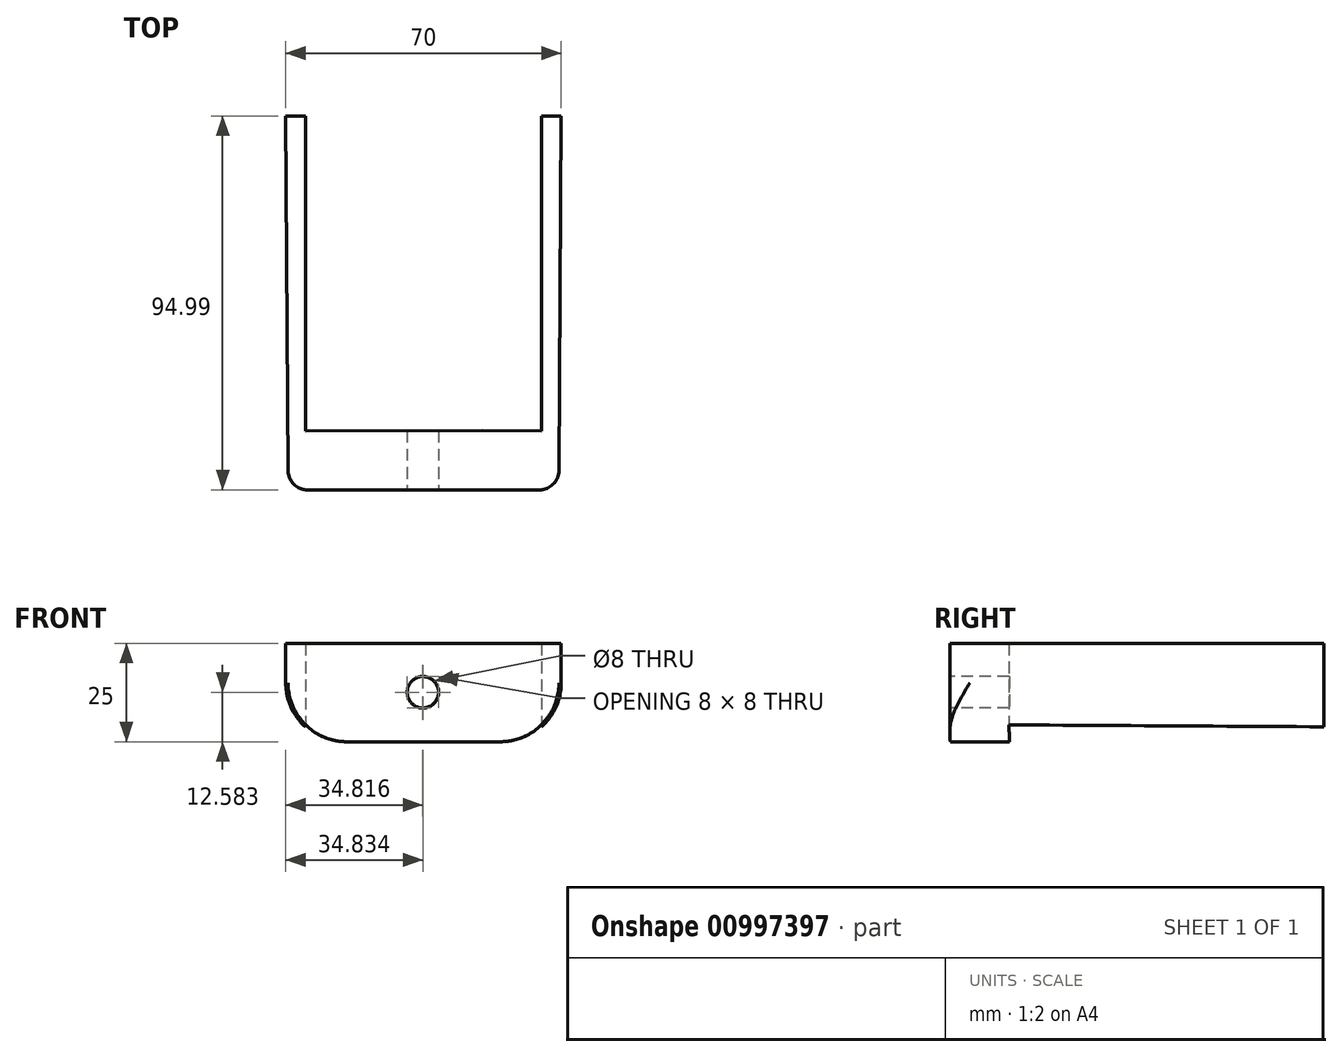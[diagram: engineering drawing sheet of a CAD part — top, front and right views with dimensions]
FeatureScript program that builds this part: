
annotation { "Feature Type Name" : "Feature", "Feature Type Description" : "" }
export const myFeature = defineFeature(function(context is Context, id is Id, definition is map)
    precondition{}
    {
        {
            var Q0;
            Q0=qCreatedBy(makeId("Top.planeOp"),FACE);
            var sketch = newSketch(context, id + "F0", { "sketchPlane" : qUnion([Q0])});
            skLineSegment(sketch, "E0.left", {"start": v(9.87, 79.3) * mm, "end": v(10.45, 169.3) * mm});
            skPoint(sketch, "E1.visualSharp", {"position": v(9.46, 15.57) * mm});
            skArc(sketch, "E1.filletArc", {"start": v(4.87, 74.34) * mm, "mid": v(8.4, 75.79) * mm, "end": v(9.87, 79.3) * mm});
            skLineSegment(sketch, "E2", {"start": v(10.45, 169.3) * mm, "end": v(5.45, 169.33) * mm});
            skLineSegment(sketch, "E3", {"start": v(5.45, 169.33) * mm, "end": v(5.45, 89.33) * mm});
            skLineSegment(sketch, "E4.MirrorCS", {"start": v(-9.55, 89.37) * mm, "end": v(5.45, 89.33) * mm});
            skLineSegment(sketch, "E5", {"start": v(4.87, 74.34) * mm, "end": v(-9.55, 74.37) * mm});
            skLineSegment(sketch, "E6.MirrorCS", {"start": v(-58.97, 79.3) * mm, "end": v(-59.55, 169.3) * mm});
            skPoint(sketch, "E7.MirrorP", {"position": v(-28.57, 15.57) * mm});
            skLineSegment(sketch, "E8.MirrorCS", {"start": v(-59.55, 169.3) * mm, "end": v(-54.55, 169.33) * mm});
            skLineSegment(sketch, "E9.MirrorCS", {"start": v(-54.55, 169.33) * mm, "end": v(-54.55, 89.33) * mm});
            skArc(sketch, "E10.MirrorCS", {"start": v(-53.98, 74.34) * mm, "mid": v(-57.5, 75.79) * mm, "end": v(-58.97, 79.3) * mm});
            skLineSegment(sketch, "E11.MirrorCS", {"start": v(-53.98, 74.34) * mm, "end": v(-39.55, 74.37) * mm});
            skLineSegment(sketch, "E12.MirrorCS", {"start": v(-9.55, 89.37) * mm, "end": v(-54.55, 89.33) * mm});
            skLineSegment(sketch, "E13", {"start": v(-39.55, 74.37) * mm, "end": v(-9.55, 74.37) * mm});
            skSolve(sketch);
        }
        {
            var Q0;
            {var subQ5=sQuery(id+"F0.wireOp",EDGE,"E1.filletArc");Q0=makeQuery(id+"F0.imprint","IMPRINT",FACE,{"disambiguationData":[TD([[makeQuery(id+"F0.imprint","IMPRINT",EDGE,{"derivedFrom":subQ5}),1.0]])]});}
            var Q1;
            {var subQ2=sQuery(id+"F0.wireOp",EDGE,"E0.left");Q1=makeQuery(id+"F0.imprint","IMPRINT",FACE,{"disambiguationData":[TD([[makeQuery(id+"F0.imprint","IMPRINT",EDGE,{"derivedFrom":subQ2}),1.0]])]});}
            var Q2;
            {var subQ3=sQuery(id+"F0.wireOp",EDGE,"E6.MirrorCS");Q2=makeQuery(id+"F0.imprint","IMPRINT",FACE,{"disambiguationData":[TD([[makeQuery(id+"F0.imprint","IMPRINT",EDGE,{"derivedFrom":subQ3}),-1.0]])]});}
            var Q3;
            {var subQ4=sQuery(id+"F0.wireOp",EDGE,"E10.MirrorCS");Q3=makeQuery(id+"F0.imprint","IMPRINT",FACE,{"disambiguationData":[TD([[makeQuery(id+"F0.imprint","IMPRINT",EDGE,{"derivedFrom":subQ4}),-1.0]])]});}
            extrude(context, id + "F1", {"entities" : qUnion([Q0, Q1, Q2, Q3]), "depth" : 25 * mm, "offsetDistance" : 25 * mm});
        }
        {
            var Q0;
            Q0=makeQuery(id+"F1.opExtrude","SWEPT_FACE",FACE,{"disambiguationData":[OSD([sQuery(id+"F0.wireOp",EDGE,"E11.MirrorCS")])]});
            var sketch = newSketch(context, id + "F2", { "sketchPlane" : qUnion([Q0])});
            skCircle(sketch, "E14", {"center": v(-24.52, 12.58) * mm, "radius": 4 * mm});
            skSolve(sketch);
        }
        {
            var Q0;
            {var subQ0=sQuery(id+"F2.wireOp",EDGE,"E14");var subQ1=makeQuery(id+"F1.opExtrude","SWEPT_EDGE",EDGE,{"disambiguationData":[OSD([sQuery(id+"F0.wireOp",EDGE,"N1CpDyrb-BCyz-cdjO-E7GZ-U4OTjqENN9a4"),sQuery(id+"F0.wireOp",EDGE,"E5"),sQuery(id+"F0.wireOp",EDGE,"E11.MirrorCS")])]});var subQ2=makeQuery(id+"F2.imprint","INTERSECT",VERTEX,{"disambiguationData":[OD(0.0)],"derivedFrom":[subQ1,subQ0]});Q0=makeQuery(id+"F2.imprint","IMPRINT",FACE,{"disambiguationData":[TD([[makeQuery(id+"F2.imprint","IMPRINT",EDGE,{"disambiguationData":[TD([[subQ2,-1.0]])],"derivedFrom":subQ0}),1.0]])]});}
            var Q1;
            {var subQ0=sQuery(id+"F2.wireOp",EDGE,"E14");var subQ1=makeQuery(id+"F1.opExtrude","SWEPT_EDGE",EDGE,{"disambiguationData":[OSD([sQuery(id+"F0.wireOp",EDGE,"N1CpDyrb-BCyz-cdjO-E7GZ-U4OTjqENN9a4"),sQuery(id+"F0.wireOp",EDGE,"E5"),sQuery(id+"F0.wireOp",EDGE,"E11.MirrorCS")])]});var subQ2=makeQuery(id+"F2.imprint","INTERSECT",VERTEX,{"disambiguationData":[OD(0.0)],"derivedFrom":[subQ1,subQ0]});Q1=makeQuery(id+"F2.imprint","IMPRINT",FACE,{"disambiguationData":[TD([[makeQuery(id+"F2.imprint","IMPRINT",EDGE,{"disambiguationData":[TD([[subQ2,1.0]])],"derivedFrom":subQ0}),1.0]])]});}
            extrude(context, id + "F3", {"entities" : qUnion([Q0, Q1]), "operationType" : NewBodyOperationType.REMOVE, "oppositeDirection" : true, "depth" : 17.8 * mm, "offsetDistance" : 25 * mm});
        }
        {
            var Q0;
            Q0=makeQuery(id+"F3.boolean.opBoolean","COPY",FACE,{"derivedFrom":makeQuery(id+"F3.opExtrude","CAP_FACE",FACE,{"disambiguationData":[OSD([sQuery(id+"F2.wireOp",EDGE,"E14")])],"isStart":true})});
            extrude(context, id + "F4", {"entities" : qUnion([Q0]), "operationType" : NewBodyOperationType.REMOVE, "oppositeDirection" : true, "depth" : 25 * mm, "offsetDistance" : 25 * mm});
        }
        {
            var Q0;
            Q0=makeQuery(id+"F1.opExtrude","CAP_EDGE",EDGE,{"disambiguationData":[OSD([sQuery(id+"F0.wireOp",EDGE,"E0.left")])],"isStart":true});
            fillet(context, id + "F5", {"entities" : qUnion([Q0]), "radius" : 15 * mm, "tangentPropagation" : true, "allowEdgeOverflow" : false});
        }
        {
            var Q0;
            Q0=makeQuery(id+"F1.opExtrude","CAP_EDGE",EDGE,{"disambiguationData":[OSD([sQuery(id+"F0.wireOp",EDGE,"E6.MirrorCS")])],"isStart":true});
            fillet(context, id + "F6", {"entities" : qUnion([Q0]), "radius" : 15 * mm, "tangentPropagation" : true, "allowEdgeOverflow" : false});
        }
    });
